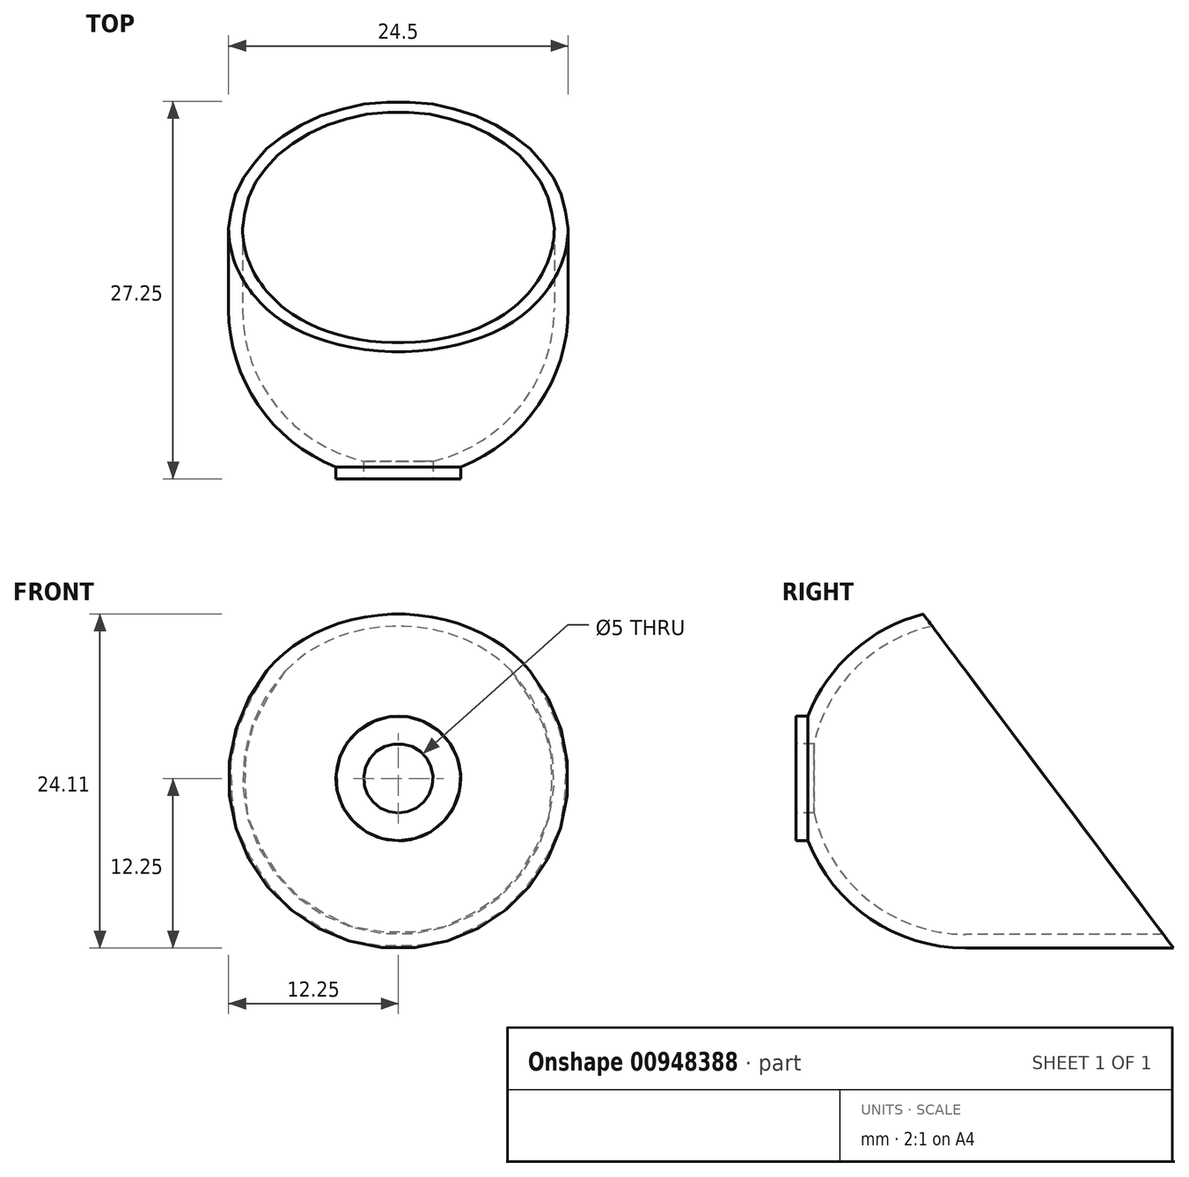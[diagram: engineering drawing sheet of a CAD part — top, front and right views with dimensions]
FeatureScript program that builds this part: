
annotation { "Feature Type Name" : "Feature", "Feature Type Description" : "" }
export const myFeature = defineFeature(function(context is Context, id is Id, definition is map)
    precondition{}
    {
        {
            var Q0;
            Q0=qCreatedBy(makeId("Right.planeOp"),FACE);
            var sketch = newSketch(context, id + "F0", { "sketchPlane" : qUnion([Q0])});
            skLineSegment(sketch, "E0", {"start": v(0, 16.8) * mm, "end": v(0, -17.58) * mm, "construction": true});
            skLineSegment(sketch, "E1", {"start": v(-25.53, 0) * mm, "end": v(25.14, 0) * mm, "construction": true});
            skArc(sketch, "E2", {"start": v(0, 12.25) * mm, "mid": v(-12.25, 0) * mm, "end": v(0, -12.25) * mm});
            skLineSegment(sketch, "E3", {"start": v(15, -12.25) * mm, "end": v(15, 12.25) * mm});
            skLineSegment(sketch, "E4", {"start": v(-12.25, 0) * mm, "end": v(15, 0) * mm});
            skLineSegment(sketch, "E5", {"start": v(0, -12.25) * mm, "end": v(15, -12.25) * mm});
            skLineSegment(sketch, "E6", {"start": v(0, 12.25) * mm, "end": v(15, 12.25) * mm});
            skLineSegment(sketch, "E7", {"start": v(0, 11.25) * mm, "end": v(16.65, 11.25) * mm});
            skLineSegment(sketch, "E8", {"start": v(16.65, -11.25) * mm, "end": v(0, -11.25) * mm});
            skLineSegment(sketch, "E9", {"start": v(16.65, 11.25) * mm, "end": v(16.65, -11.25) * mm});
            skArc(sketch, "E10", {"start": v(0, 11.25) * mm, "mid": v(-11.25, 0) * mm, "end": v(0, -11.25) * mm});
            skLineSegment(sketch, "E11", {"start": v(-12.25, 2.5) * mm, "end": v(-10.97, 2.5) * mm});
            skLineSegment(sketch, "E12", {"start": v(-12.2, -2.5) * mm, "end": v(-10.97, -2.5) * mm});
            skLineSegment(sketch, "E13", {"start": v(-12.25, 4.5) * mm, "end": v(-10.31, 4.5) * mm});
            skLineSegment(sketch, "E14", {"start": v(-12.17, -4.5) * mm, "end": v(-10.31, -4.5) * mm});
            skLineSegment(sketch, "E15", {"start": v(-12.25, 2.5) * mm, "end": v(-12.25, 4.5) * mm});
            skLineSegment(sketch, "E16", {"start": v(-12.2, -2.5) * mm, "end": v(-12.17, -4.5) * mm});
            skSolve(sketch);
        }
        {
            var Q0;
            {var subQ0=sQuery(id+"F0.wireOp",EDGE,"E6");Q0=makeQuery(id+"F0.imprint","IMPRINT",FACE,{"disambiguationData":[TD([[makeQuery(id+"F0.imprint","IMPRINT",EDGE,{"derivedFrom":subQ0}),-1.0]])]});}
            var Q1;
            {var subQ0=sQuery(id+"F0.wireOp",EDGE,"E13");var subQ1=sQuery(id+"F0.wireOp",EDGE,"E2");var subQ2=makeQuery(id+"F0.imprint","INTERSECT",VERTEX,{"derivedFrom":[subQ1,subQ0]});Q1=makeQuery(id+"F0.imprint","IMPRINT",FACE,{"disambiguationData":[TD([[makeQuery(id+"F0.imprint","IMPRINT",EDGE,{"disambiguationData":[TD([[subQ2,-1.0]])],"derivedFrom":subQ1}),1.0]])]});}
            var Q2;
            {var subQ5=sQuery(id+"F0.wireOp",EDGE,"E15");Q2=makeQuery(id+"F0.imprint","IMPRINT",FACE,{"disambiguationData":[TD([[makeQuery(id+"F0.imprint","IMPRINT",EDGE,{"derivedFrom":subQ5}),-1.0]])]});}
            var Q3;
            Q3=sQuery(id+"F0.wireOp",EDGE,"E4");
            revolve(context, id + "F1", {"surfaceOperationType" : NewSurfaceOperationType.NEW, "entities" : qUnion([Q0, Q1, Q2]), "axis" : qUnion([Q3]), "revolveType" : RevolveType.FULL});
        }
        {
            var Q0;
            Q0=qCreatedBy(makeId("Right.planeOp"),FACE);
            var sketch = newSketch(context, id + "F2", { "sketchPlane" : qUnion([Q0])});
            skLineSegment(sketch, "E17", {"start": v(-18.33, 0) * mm, "end": v(23.44, 0) * mm, "construction": true});
            skLineSegment(sketch, "E18", {"start": v(0, 15.28) * mm, "end": v(0, -14.92) * mm, "construction": true});
            skLineSegment(sketch, "E19", {"start": v(-18.33, -12.25) * mm, "end": v(24.15, -12.25) * mm, "construction": true});
            skLineSegment(sketch, "E20", {"start": v(15, 15.32) * mm, "end": v(15, -15.22) * mm, "construction": true});
            skLineSegment(sketch, "E21", {"start": v(15, -12.25) * mm, "end": v(-12.72, 24.71) * mm});
            skLineSegment(sketch, "E22", {"start": v(-12.72, 24.71) * mm, "end": v(15, 24.71) * mm});
            skLineSegment(sketch, "E23", {"start": v(15, 24.71) * mm, "end": v(15, -12.25) * mm});
            skSolve(sketch);
        }
        {
            var Q0;
            Q0=makeQuery(id+"F2.imprint","IMPRINT",FACE,{"disambiguationData":[TD([[makeQuery(id+"F2.imprint","IMPRINT",EDGE,{"derivedFrom":sQuery(id+"F2.wireOp",EDGE,"E21")}),-1.0]])]});
            extrude(context, id + "F3", {"entities" : qUnion([Q0]), "operationType" : NewBodyOperationType.REMOVE, "endBound" : BoundingType.SYMMETRIC, "depth" : 30 * mm, "offsetDistance" : 25 * mm});
        }
    });
